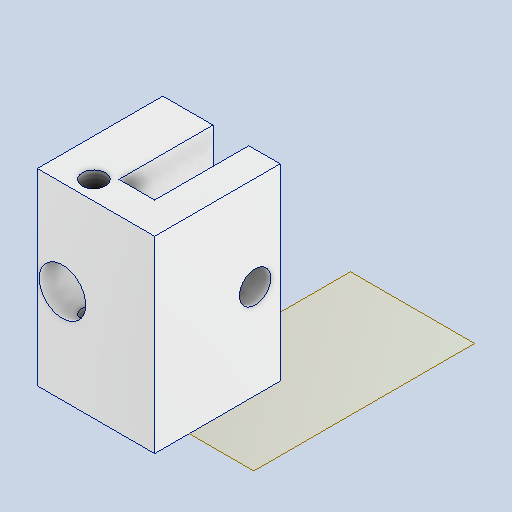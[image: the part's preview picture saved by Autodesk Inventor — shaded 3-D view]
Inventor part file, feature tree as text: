
AUTODESK INVENTOR PART (.ipt)
format: ipt  version: 2025 (Build 290162010, 162A)  size: 248,832 bytes
history: native  units: mm
features: sketch x9, hole x8, projected_geometry x4, other x3, plane x1, extrude x1, thread x1, reference x1
ambient origin geometry x8: Origin, YZ Plane, XZ Plane, XY Plane, X Axis, Y Axis, Z Axis, Center Point
bodies: Volumenkörper1 (feature_tree)
feature tree (28):
  plane  "Arbeitsebene1"
  extrude  "Extrusion1"  Depth=30.0mm TaperAngle=0.0deg
  hole  "GLHU"  [1 undecoded]
  hole  "GLHH"  [1 undecoded]
  hole  "GLHO"  [1 undecoded]
  hole  "DLHO"  [1 undecoded]
  hole  "DLHU"  [1 undecoded]
  hole  "Zentrierbolzen"  [1 undecoded]
  hole  "LK-Verschraubung"  [1 undecoded]
  hole  "seiloese"  [1 undecoded]
  thread  "Gewinde4"  [1 undecoded]
  sketch  "Skizze1"  dims[d0=5.0mm d1=8.0mm d2=5.0mm d3=20.0mm d4=2.1mm d5=30.0mm d6=0.0mm]
  reference  "Referenz1"
  sketch  "Skizze3"  dims[d15=1.567mm d16=2.5mm d17=4.0mm d18=2.0mm d19=90.0deg d20=4.0mm d21=20.594885mm d42=2.5mm]
  sketch  "Skizze6"  dims[d43=3.0mm]
  projected_geometry  "Projizierte Kontur5"
  sketch  "Skizze8"  dims[d44=2.0mm d45=6.0mm d46=4.0mm d47=2.0mm d48=90.0deg d49=5.0mm d50=20.594885mm d58=4.0mm]
  projected_geometry  "Projizierte Kontur7"
  sketch  "Skizze9"  dims[d59=4.0mm d60=6.0mm d61=7.4mm d62=14.0mm d63=90.0deg d64=8.0mm d65=20.594885mm]
  projected_geometry  "Projizierte Kontur8"
  sketch  "Skizze10"  dims[d66=1.567mm d67=2.5mm d68=4.0mm d69=2.0mm d70=90.0deg d71=4.0mm d72=20.594885mm d74=9.0mm]
  sketch  "Skizze11"  dims[d75=4.0mm]
  projected_geometry  "Projizierte Kontur9"
  sketch  "Skizze12"  dims[d76=1.567mm d77=2.5mm d78=4.0mm d79=2.0mm d80=90.0deg d81=4.0mm d82=20.594885mm]
  sketch  "Skizze13"  dims[d83=5.0mm d84=2.5mm d85=4.0mm d86=2.0mm d87=90.0deg d88=4.0mm d89=20.594885mm d90=5.0mm d91=6.0mm d92=7.4mm d93=11.0mm d94=90.0deg d95=8.0mm d96=20.594885mm d100=3.688101mm d101=9.0mm d102=4.0mm d103=2.0mm d104=90.0deg d105=8.0mm d106=20.594885mm d107=9.0mm d108=0.0mm d109=6.0mm d110=3.0mm d97=1.0mm d98=1.0mm d99=1.0mm]
  other  "<userpath>\Documents\Inventor\Krandemonstrator\Demonstrator.iam"
  other  "Demonstrator.iam"
  other  "Träger:1"
note: 9 required parameter values undecoded (feature->parameter linkage not recoverable at this tier; creation-order binding heuristic only, values carry confidence <= 0.55)
